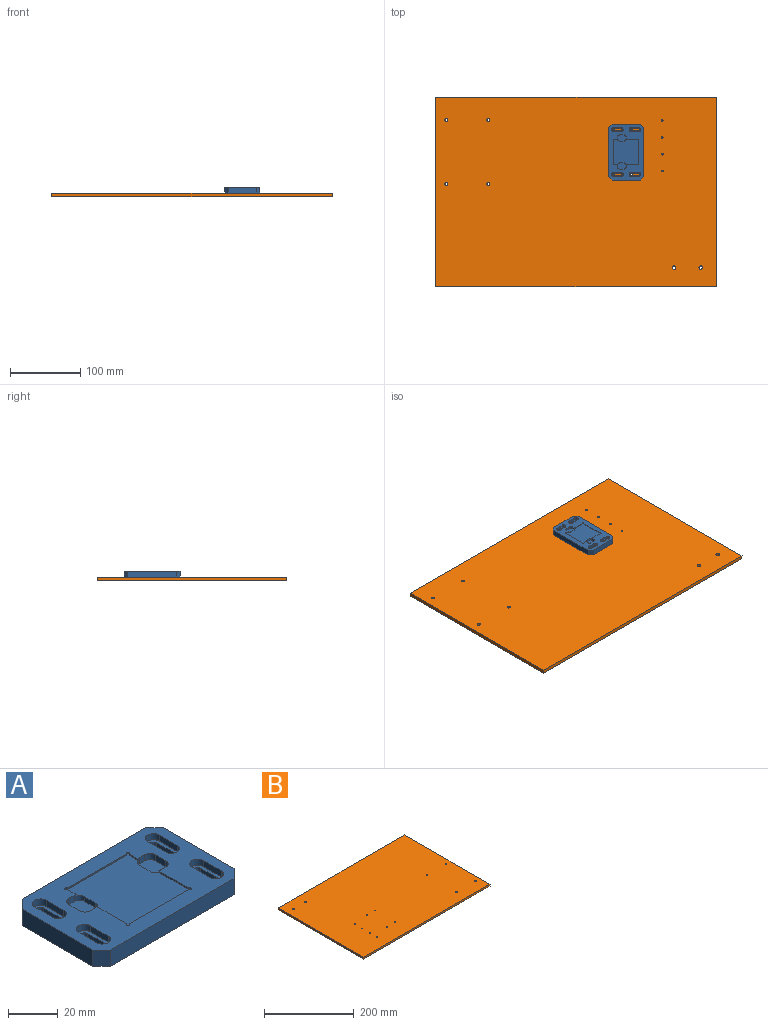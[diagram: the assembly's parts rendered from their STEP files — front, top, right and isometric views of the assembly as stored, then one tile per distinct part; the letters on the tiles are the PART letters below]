
ASSEMBLY  parts=2 mates=1
PART A: 75 faces, bbox 80x50x8 mm
  f0: cylinder r=3mm len=3mm, axis (0,0,-1), area 11.6mm2, adj f1,f43,f44,f66,f68,f69
  f1: plane 4.92x0.7mm, normal (1,0,0), area 3.4mm2, adj f0,f2,f44,f68
  f2: cylinder r=0.75mm len=1.5mm, axis (0,0,-1), area 2.5mm2, adj f1,f3,f44,f68
  f3: plane 33.5x0.7mm, normal (0,-1,0), area 23.5mm2, adj f2,f4,f44,f68
  f4: cylinder r=0.75mm len=1.5mm, axis (0,0,-1), area 2.5mm2, adj f3,f5,f44,f68
  f5: plane 4.92x0.7mm, normal (-1,0,0), area 3.4mm2, adj f4,f6,f44,f68
  f6: cylinder r=3mm len=3mm, axis (0,0,-1), area 11.6mm2, adj f5,f7,f44,f67,f68,f70
  f7: plane 3x3mm, normal (0,-1,0), area 9mm2, adj f6,f8,f44,f70
  f8: cylinder r=3mm len=3mm, axis (0,0,-1), area 14.1mm2, adj f7,f9,f44,f70
  f9: plane 6x3mm, normal (-1,0,0), area 18mm2, adj f8,f10,f44,f70
  f10: cylinder r=3mm len=3mm, axis (0,0,-1), area 14.1mm2, adj f9,f11,f44,f70
  f11: plane 3x3mm, normal (0,1,0), area 9mm2, adj f10,f12,f44,f70
  f12: cylinder r=3mm len=3mm, axis (0,0,-1), area 11.6mm2, adj f11,f13,f44,f67,f68,f70
  f13: plane 16.92x0.7mm, normal (-1,0,0), area 11.8mm2, adj f12,f14,f44,f68
  f14: cylinder r=0.75mm len=1.5mm, axis (0,0,-1), area 2.5mm2, adj f13,f15,f44,f68
  f15: plane 33.5x0.7mm, normal (0,1,0), area 23.5mm2, adj f14,f16,f44,f68
  f16: cylinder r=0.75mm len=1.5mm, axis (0,0,-1), area 2.5mm2, adj f15,f17,f44,f68
  f17: plane 16.92x0.7mm, normal (1,0,0), area 11.8mm2, adj f16,f18,f44,f68
  f18: cylinder r=3mm len=3mm, axis (0,0,-1), area 11.6mm2, adj f17,f19,f44,f66,f68,f69
  f19: plane 3x3mm, normal (0,1,0), area 9mm2, adj f18,f20,f44,f69
  f20: cylinder r=3mm len=3mm, axis (0,0,-1), area 14.1mm2, adj f19,f21,f44,f69
  f21: plane 6x3mm, normal (1,0,0), area 18mm2, adj f20,f22,f44,f69
  f22: cylinder r=3mm len=3mm, axis (0,0,-1), area 14.1mm2, adj f21,f43,f44,f69
  f23: plane 10x3mm, normal (1,0,0), area 30mm2, adj f24,f38,f44,f65
  f24: cylinder r=3.25mm len=6.5mm, axis (0,0,-1), area 30.6mm2, adj f23,f25,f44,f65
  f25: plane 10x3mm, normal (-1,0,0), area 30mm2, adj f24,f38,f44,f65
  f26: plane 10x3mm, normal (1,0,0), area 30mm2, adj f27,f39,f44,f60
  f27: cylinder r=3.25mm len=6.5mm, axis (0,0,-1), area 30.6mm2, adj f26,f28,f44,f60
  f28: plane 10x3mm, normal (-1,0,0), area 30mm2, adj f27,f39,f44,f60
  f29: plane 10x3mm, normal (1,0,0), area 30mm2, adj f30,f40,f44,f55
  f30: cylinder r=3.25mm len=6.5mm, axis (0,0,-1), area 30.6mm2, adj f29,f31,f44,f55
  f31: plane 10x3mm, normal (-1,0,0), area 30mm2, adj f30,f40,f44,f55
  f32: plane 10x3mm, normal (1,0,0), area 30mm2, adj f33,f41,f44,f50
  f33: cylinder r=3.25mm len=6.5mm, axis (0,0,-1), area 30.6mm2, adj f32,f34,f44,f50
  f34: plane 10x3mm, normal (-1,0,0), area 30mm2, adj f33,f41,f44,f50
  f35: plane 40x8mm, normal (-1,0,0), area 320mm2, adj f44,f45,f73,f74
  f36: plane 70x8mm, normal (0,-1,0), area 560mm2, adj f44,f45,f72,f73
  f37: plane 40x8mm, normal (1,0,0), area 320mm2, adj f44,f45,f71,f72
  f38: cylinder r=3.25mm len=6.5mm, axis (0,0,-1), area 30.6mm2, adj f23,f25,f44,f65
  f39: cylinder r=3.25mm len=6.5mm, axis (0,0,-1), area 30.6mm2, adj f26,f28,f44,f60
  f40: cylinder r=3.25mm len=6.5mm, axis (0,0,-1), area 30.6mm2, adj f29,f31,f44,f55
  f41: cylinder r=3.25mm len=6.5mm, axis (0,0,-1), area 30.6mm2, adj f32,f34,f44,f50
  f42: plane 70x8mm, normal (0,1,0), area 560mm2, adj f44,f45,f71,f74
  f43: plane 3x3mm, normal (0,-1,0), area 9mm2, adj f0,f22,f44,f69
  f44: plane 80x50mm, normal (0,0,1), area 2166.9mm2, adj f0,f1,f2,f3,f4,f5,f6,f7
  f45: plane 80x50mm, normal (0,0,-1), area 3777.7mm2, adj f35,f36,f37,f42,f46,f47,f48,f49
  f46: plane 10x5mm, normal (1,0,0), area 50mm2, adj f45,f47,f49,f50
  f47: cylinder r=1.7mm len=5mm, axis (0,0,-1), area 26.7mm2, adj f45,f46,f48,f50
  f48: plane 10x5mm, normal (-1,0,0), area 50mm2, adj f45,f47,f49,f50
  f49: cylinder r=1.7mm len=5mm, axis (0,0,-1), area 26.7mm2, adj f45,f46,f48,f50
  f50: plane 16.5x6.5mm, normal (0,0,1), area 55.1mm2, adj f32,f33,f34,f41,f46,f47,f48,f49
  f51: plane 10x5mm, normal (1,0,0), area 50mm2, adj f45,f52,f54,f55
  f52: cylinder r=1.7mm len=5mm, axis (0,0,-1), area 26.7mm2, adj f45,f51,f53,f55
  f53: plane 10x5mm, normal (-1,0,0), area 50mm2, adj f45,f52,f54,f55
  f54: cylinder r=1.7mm len=5mm, axis (0,0,-1), area 26.7mm2, adj f45,f51,f53,f55
  f55: plane 16.5x6.5mm, normal (0,0,1), area 55.1mm2, adj f29,f30,f31,f40,f51,f52,f53,f54
  f56: cylinder r=1.7mm len=5mm, axis (0,0,-1), area 26.7mm2, adj f45,f57,f59,f60
  f57: plane 10x5mm, normal (1,0,0), area 50mm2, adj f45,f56,f58,f60
  f58: cylinder r=1.7mm len=5mm, axis (0,0,-1), area 26.7mm2, adj f45,f57,f59,f60
  f59: plane 10x5mm, normal (-1,0,0), area 50mm2, adj f45,f56,f58,f60
  f60: plane 16.5x6.5mm, normal (0,0,1), area 55.1mm2, adj f26,f27,f28,f39,f56,f57,f58,f59
  f61: cylinder r=1.7mm len=5mm, axis (0,0,-1), area 26.7mm2, adj f45,f62,f64,f65
  f62: plane 10x5mm, normal (1,0,0), area 50mm2, adj f45,f61,f63,f65
  f63: cylinder r=1.7mm len=5mm, axis (0,0,-1), area 26.7mm2, adj f45,f62,f64,f65
  f64: plane 10x5mm, normal (-1,0,0), area 50mm2, adj f45,f61,f63,f65
  f65: plane 16.5x6.5mm, normal (0,0,1), area 55.1mm2, adj f23,f24,f25,f38,f61,f62,f63,f64
  f66: plane 6x2.3mm, normal (-1,0,0), area 13.8mm2, adj f0,f18,f68,f69
  f67: plane 6x2.3mm, normal (1,0,0), area 13.8mm2, adj f6,f12,f68,f70
  f68: plane 36.5x36.5mm, normal (0,0,1), area 1189.8mm2, adj f0,f1,f2,f3,f4,f5,f6,f12
  f69: plane 12x9mm, normal (0,0,1), area 100.3mm2, adj f0,f18,f19,f20,f21,f22,f43,f66
  f70: plane 12x9mm, normal (0,0,1), area 100.3mm2, adj f6,f7,f8,f9,f10,f11,f12,f67
  f71: plane 8x5mm, normal (0.71,0.71,0), area 56.6mm2, adj f37,f42,f44,f45
  f72: plane 8x5mm, normal (0.71,-0.71,0), area 56.6mm2, adj f36,f37,f44,f45
  f73: plane 8x5mm, normal (-0.71,-0.71,0), area 56.6mm2, adj f35,f36,f44,f45
  f74: plane 8x5mm, normal (-0.71,0.71,0), area 56.6mm2, adj f35,f42,f44,f45
PART B: 20 faces, bbox 400x270x5 mm
  f0: plane 270x5mm, normal (-1,0,0), area 1350mm2, adj f1,f3,f4,f5
  f1: plane 400x5mm, normal (0,-1,0), area 2000mm2, adj f0,f2,f4,f5
  f2: plane 270x5mm, normal (1,0,0), area 1350mm2, adj f1,f3,f4,f5
  f3: plane 400x5mm, normal (0,1,0), area 2000mm2, adj f0,f2,f4,f5
  f4: plane 400x270mm, normal (0,0,1), area 107866mm2, adj f0,f1,f2,f3,f6,f7,f8,f9
  f5: plane 400x270mm, normal (0,0,-1), area 107866mm2, adj f0,f1,f2,f3,f6,f7,f8,f9
  f6: cylinder r=2.5mm len=5mm, axis (0,0,-1), area 78.5mm2, adj f4,f5
  f7: cylinder r=2.5mm len=5mm, axis (0,0,-1), area 78.5mm2, adj f4,f5
  f8: cylinder r=1.25mm len=5mm, axis (0,0,-1), area 39.3mm2, adj f4,f5
  f9: cylinder r=1.25mm len=5mm, axis (0,0,-1), area 39.3mm2, adj f4,f5
  f10: cylinder r=1.25mm len=5mm, axis (0,0,-1), area 39.3mm2, adj f4,f5
  f11: cylinder r=1.25mm len=5mm, axis (0,0,-1), area 39.3mm2, adj f4,f5
  f12: cylinder r=1.25mm len=5mm, axis (0,0,-1), area 39.3mm2, adj f4,f5
  f13: cylinder r=1.25mm len=5mm, axis (0,0,-1), area 39.3mm2, adj f4,f5
  f14: cylinder r=1.25mm len=5mm, axis (0,0,-1), area 39.3mm2, adj f4,f5
  f15: cylinder r=1.25mm len=5mm, axis (0,0,-1), area 39.3mm2, adj f4,f5
  f16: cylinder r=2.1mm len=5mm, axis (0,0,-1), area 66mm2, adj f4,f5
  f17: cylinder r=2.1mm len=5mm, axis (0,0,-1), area 66mm2, adj f4,f5
  f18: cylinder r=2.1mm len=5mm, axis (0,0,-1), area 66mm2, adj f4,f5
  f19: cylinder r=2.1mm len=5mm, axis (0,0,-1), area 66mm2, adj f4,f5
PLACE A rot(axis=(0,0,1),90deg) t=(126.25,-193.05,28.7)mm
PLACE B rot(axis=(0,0,-1),180deg) t=(54.75,-250.05,23.7)mm
MATE fastened B.f12 <-> A.f24  axis (0,0,1) through (133.75,-161.05,28.7)mm
